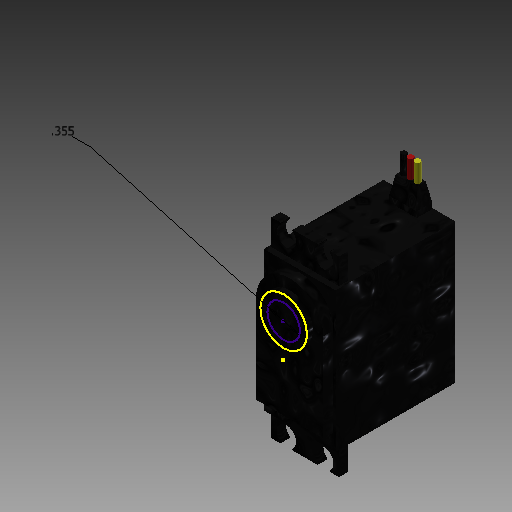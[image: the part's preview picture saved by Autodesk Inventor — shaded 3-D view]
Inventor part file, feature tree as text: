
AUTODESK INVENTOR PART (.ipt)
format: ipt  version: 2017 (Build 210142000, 142)  size: 237,568 bytes
history: native  units: in
note: dims shown in document units (in); Inventor stores cm internally (conversion verified against a paired STEP export)
features: sketch x10, extrude x9, other x4, fillet x2, plane x1, mirror x1, projected_geometry x1, hole x1
ambient origin geometry x8: Origin, YZ Plane, XZ Plane, XY Plane, X Axis, Y Axis, Z Axis, Center Point
bodies: Body1 (feature_tree), Body2 (feature_tree), Body3 (feature_tree)
feature tree (29):
  other  "Servo"
  other  "Blocks"
  extrude  "Extrusion1"  Depth=1.525in
  extrude  "Extrusion2"  Depth=0.025in
  extrude  "Extrusion3"  Depth=0.17in
  fillet  "Fillet1"  Radius=0.11in
  plane  "Work Plane1"
  extrude  "Extrusion4"  Depth=0.07in
  fillet  "Fillet2"  Radius=0.07in
  mirror  "Mirror1"
  extrude  "Extrusion5"  [1 undecoded]
  extrude  "Extrusion6"  Depth=0.28in
  extrude  "Extrusion7"  Depth=0.1in
  extrude  "Extrusion8"  Depth=0.1in TaperAngle=0.0deg
  extrude  "Extrusion9"  Depth=0.3in
  sketch  "Sketch25"  dims[d27=0.17in d28=0.01in d29=0.0625in d30=0.0in d31=0.2in d32=-0.0687in d33=0.0625in d34=0.2in d35=0.0in d36=0.0625in d37=0.04in d38=0.2in d39=0.0in d40=0.0625in d41=0.04in d42=0.2in d43=0.0in d140=0.6299in d141=0.1457in d142=0.6299in d143=0.6299in d144=0.315in d145=0.355in]
  sketch  "Sketch1"  dims[d0=0.782in d1=1.525in]
  sketch  "Sketch2"  dims[d2=1.305in d3=0.0in d4=0.025in]
  sketch  "Sketch3"  dims[d5=0.025in d6=0.17in d7=0.11in d8=0.0in]
  sketch  "Sketch4"  dims[d9=0.508in d11=0.391in d12=0.07in d13=0.0in]
  sketch  "Sketch5"  dims[d14=0.366in d15=-0.16in]
  sketch  "Sketch6"  dims[d16=0.737in d18=0.28in]
  sketch  "Sketch7"  dims[d19=0.1in d20=0.21in d21=0.165in]
  other  "Red wire"
  sketch  "Sketch8"  dims[d22=0.165in d23=0.1in d24=0.0in]
  sketch  "Sketch9"  dims[d25=0.01in d26=0.3in]
  other  "Yellow Wire"
  projected_geometry  "Project Cut Edges1"
  hole  "Hole Pattern 4"  [1 undecoded]
note: 2 required parameter values undecoded (feature->parameter linkage not recoverable at this tier; creation-order binding heuristic only, values carry confidence <= 0.55)
